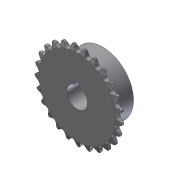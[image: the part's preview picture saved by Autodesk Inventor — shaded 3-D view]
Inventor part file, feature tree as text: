
AUTODESK INVENTOR PART (.ipt)
format: ipt  version: 2012 (Build 160160000, 160)  size: 670,720 bytes
history: native  units: in
note: dims shown in document units (in); Inventor stores cm internally (conversion verified against a paired STEP export)
features: other x2, extrude x2, sketch x2, imported_body x1
ambient origin geometry x8: Origin, YZ Plane, XZ Plane, XY Plane, X Axis, Y Axis, Z Axis, Center Point
feature tree (7):
  parser-record x1  (decoder bookkeeping rows leaked as tree rows — omitted from the tree; the rows remain in map.json)
  other  "6793K1801"
  extrude  "Extrusion1"  Depth=1.0in TaperAngle=0.0deg
  extrude  "Extrusion2"  Depth=0.125in
  imported_body  "Base1"
  sketch  "Sketch1"  dims[d0=0.5in d1=1.0in d2=0.0in]
  sketch  "Sketch2"  dims[d3=0.0625in d4=0.125in d5=1.0in d6=0.0in]
